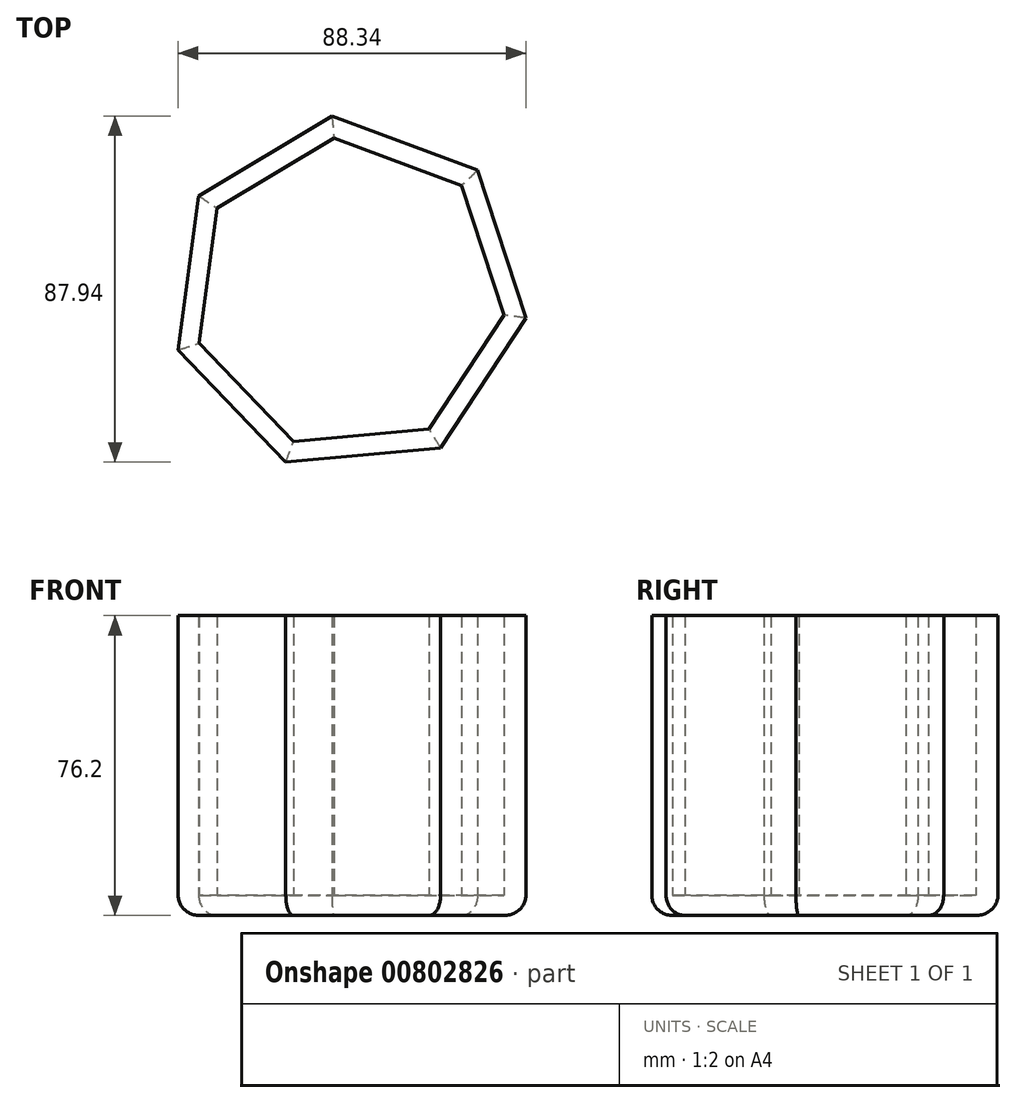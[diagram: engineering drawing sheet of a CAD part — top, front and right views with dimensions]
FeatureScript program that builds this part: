
annotation { "Feature Type Name" : "Feature", "Feature Type Description" : "" }
export const myFeature = defineFeature(function(context is Context, id is Id, definition is map)
    precondition{}
    {
        {
            var Q0;
            Q0=qCreatedBy(makeId("Top.planeOp"),FACE);
            var sketch = newSketch(context, id + "F0", { "sketchPlane" : qUnion([Q0])});
            skCircle(sketch, "E0.cCircle", {"center": v(0, 0) * mm, "radius": 45.5 * mm, "construction": true});
            skLineSegment(sketch, "E0.0", {"start": v(-15.9, -42.63) * mm, "end": v(-43.24, -14.15) * mm});
            skLineSegment(sketch, "E0.1", {"start": v(-43.24, -14.15) * mm, "end": v(-38.02, 24.99) * mm});
            skLineSegment(sketch, "E0.2", {"start": v(-38.02, 24.99) * mm, "end": v(-4.17, 45.3) * mm});
            skLineSegment(sketch, "E0.3", {"start": v(-4.17, 45.3) * mm, "end": v(32.82, 31.5) * mm});
            skLineSegment(sketch, "E0.4", {"start": v(32.82, 31.5) * mm, "end": v(45.1, -6.02) * mm});
            skLineSegment(sketch, "E0.5", {"start": v(45.1, -6.02) * mm, "end": v(23.41, -39.01) * mm});
            skLineSegment(sketch, "E0.6", {"start": v(23.41, -39.01) * mm, "end": v(-15.9, -42.63) * mm});
            skSolve(sketch);
        }
        {
            var Q0;
            Q0 = qSketchRegion(id + "F0", true);
            extrude(context, id + "F1", {"entities" : qUnion([Q0]), "depth" : 76.2 * mm, "offsetDistance" : 25.4 * mm});
        }
        {
            var Q0;
            Q0=makeQuery(id+"F1.opExtrude","CAP_FACE",FACE,{"disambiguationData":[OSD([sQuery(id+"F0.wireOp",EDGE,"E0.0"),sQuery(id+"F0.wireOp",EDGE,"E0.1"),sQuery(id+"F0.wireOp",EDGE,"E0.2"),sQuery(id+"F0.wireOp",EDGE,"E0.3"),sQuery(id+"F0.wireOp",EDGE,"E0.4"),sQuery(id+"F0.wireOp",EDGE,"E0.5"),sQuery(id+"F0.wireOp",EDGE,"E0.6")])],"isStart":false});
            shell(context, id + "F2", {"entities" : qUnion([Q0]), "thickness" : 5.08 * mm});
        }
        {
            var Q0;
            Q0=makeQuery(id+"F1.opExtrude","CAP_EDGE",EDGE,{"disambiguationData":[OSD([sQuery(id+"F0.wireOp",EDGE,"E0.6")])],"isStart":true});
            var Q1;
            Q1=makeQuery(id+"F1.opExtrude","CAP_EDGE",EDGE,{"disambiguationData":[OSD([sQuery(id+"F0.wireOp",EDGE,"E0.5")])],"isStart":true});
            var Q2;
            Q2=makeQuery(id+"F1.opExtrude","CAP_EDGE",EDGE,{"disambiguationData":[OSD([sQuery(id+"F0.wireOp",EDGE,"E0.4")])],"isStart":true});
            var Q3;
            Q3=makeQuery(id+"F1.opExtrude","CAP_EDGE",EDGE,{"disambiguationData":[OSD([sQuery(id+"F0.wireOp",EDGE,"E0.3")])],"isStart":true});
            var Q4;
            Q4=makeQuery(id+"F1.opExtrude","CAP_EDGE",EDGE,{"disambiguationData":[OSD([sQuery(id+"F0.wireOp",EDGE,"E0.2")])],"isStart":true});
            var Q5;
            Q5=makeQuery(id+"F1.opExtrude","CAP_EDGE",EDGE,{"disambiguationData":[OSD([sQuery(id+"F0.wireOp",EDGE,"E0.1")])],"isStart":true});
            var Q6;
            Q6=makeQuery(id+"F1.opExtrude","CAP_EDGE",EDGE,{"disambiguationData":[OSD([sQuery(id+"F0.wireOp",EDGE,"E0.0")])],"isStart":true});
            fillet(context, id + "F3", {"entities" : qUnion([Q0, Q1, Q2, Q3, Q4, Q5, Q6]), "radius" : 5.08 * mm, "tangentPropagation" : true, "allowEdgeOverflow" : false});
        }
    });
